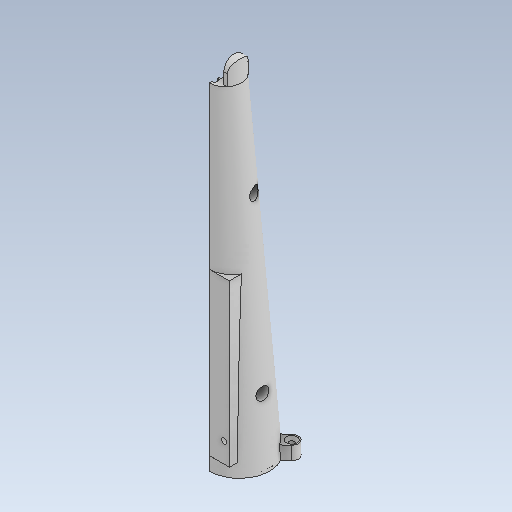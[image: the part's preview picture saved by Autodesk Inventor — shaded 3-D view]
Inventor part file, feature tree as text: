
AUTODESK INVENTOR PART (.ipt)
format: ipt  version: 2021 (Build 250183000, 183)  size: 1,118,208 bytes
history: native  units: mm
features: sketch x40, extrude x38, plane x17, fillet x9, hole x3, thread x3, loft x2, revolve x2, other x1
ambient origin geometry x8: Origin, YZ Plane, XZ Plane, XY Plane, X Axis, Y Axis, Z Axis, Center Point
bodies: Body1 (feature_tree)
feature tree (115):
  other  "Sólido1"
  plane  "Plano de trabajo1"
  plane  "Plano de trabajo2"
  plane  "Plano de trabajo4"
  plane  "Plano de trabajo5"
  plane  "Plano de trabajo6"
  sketch  "Boceto1"  dims[d1=250.0mm d2=0.0mm d3=-80.0mm d4=-110.0mm]
  sketch  "Boceto2"  dims[d5=-140.0mm d7=-0.0mm d8=2.0mm]
  sketch  "Boceto3"  dims[d9=140.0mm d10=250.0mm]
  sketch  "Boceto4"  dims[d11=24.0mm d22=0.0mm d23=90.0deg d24=0.0mm d25=90.0deg]
  sketch  "Boceto6"  dims[d44=45.0mm d49=29.11157mm]
  sketch  "Boceto7"  dims[d50=29.11157mm d53=29.11157mm]
  loft  "Solevación1"
  fillet  "Empalme2"  [1 undecoded]
  extrude  "Extrusión1"  TaperAngle=0.0deg  [1 undecoded]
  fillet  "Empalme5"  Radius=2.0mm
  plane  "Plano de trabajo7"
  extrude  "Extrusión2"  Depth=250.0mm
  plane  "Plano de trabajo8"
  plane  "Plano de trabajo9"
  loft  "Solevación9"
  plane  "Plano de trabajo10"
  extrude  "Extrusión3"  Depth=29.11157mm
  plane  "Plano de trabajo11"
  revolve  "Revolución1"  [1 undecoded]
  revolve  "Revolución2"  [1 undecoded]
  extrude  "Extrusión4"  Depth=32.5mm
  plane  "Plano de trabajo12"
  extrude  "Extrusión5"  Depth=44.747934mm
  plane  "Plano de trabajo13"
  plane  "Plano de trabajo14"
  extrude  "Extrusión6"  Depth=42.747934mm
  extrude  "Extrusión7"  Depth=42.747934mm
  extrude  "Extrusión8"  Depth=13.0mm
  extrude  "Extrusión11"  Depth=6.5mm
  extrude  "Extrusión9"  Depth=7.75mm
  extrude  "Extrusión10"  Depth=16.0mm
  extrude  "Extrusión12"  Depth=12.0mm
  sketch  "Boceto30"  dims[d160=-19.75mm d161=0.0mm]
  extrude  "Extrusión13"  Depth=7.75mm
  extrude  "Extrusión14"  Depth=6.5mm
  extrude  "Extrusión15"  TaperAngle=0.0deg  [1 undecoded]
  hole  "Agujero1"  [1 undecoded]
  thread  "Rosca1"  [1 undecoded]
  extrude  "Extrusión16"  Depth=2.0mm
  plane  "Plano de trabajo16"
  extrude  "Extrusión17"  TaperAngle=0.0deg  [1 undecoded]
  extrude  "Extrusión18"  TaperAngle=0.0deg  [1 undecoded]
  plane  "Plano de trabajo17"
  sketch  "Boceto46"  dims[d185=2.0mm d187=1.0mm]
  hole  "Agujero2"  [1 undecoded]
  hole  "Agujero3"  [1 undecoded]
  plane  "Plano de trabajo19"
  sketch  "Boceto50"  dims[d193=0.25mm d194=90.0deg]
  extrude  "Extrusión22"  Depth=12.0mm
  extrude  "Extrusión23"  [1 undecoded]
  extrude  "Extrusión24"  Depth=0.75mm
  plane  "Plano de trabajo20"
  extrude  "Extrusión25"  Depth=1.0mm
  fillet  "Empalme6"  Radius=11.0mm
  fillet  "Empalme7"  Radius=17.453293mm
  sketch  "Boceto49"  dims[d191=2.0mm d192=0.25mm]
  extrude  "Extrusión29"  Depth=0.75mm
  extrude  "Extrusión30"  Depth=0.25mm
  sketch  "Boceto44"  dims[d181=0.75mm d182=0.25mm]
  sketch  "Boceto47"  dims[d189=3.0mm d190=2.0mm]
  extrude  "Extrusión26"  Depth=0.25mm
  extrude  "Extrusión27"  Depth=2.0mm
  extrude  "Extrusión28"  Depth=2.0mm
  sketch  "Boceto45"  dims[d183=1.0mm d184=0.25mm]
  extrude  "Extrusión31"  Depth=2.0mm
  extrude  "Extrusión32"  TaperAngle=90.0deg  [1 undecoded]
  extrude  "Extrusión33"  [1 undecoded]
  extrude  "Extrusión34"  Depth=20.0mm
  extrude  "Extrusión35"  Depth=2.0mm
  thread  "Rosca2"  [1 undecoded]
  thread  "Rosca3"  [1 undecoded]
  fillet  "Empalme8"  [1 undecoded]
  fillet  "Empalme9"  Radius=0.5mm
  fillet  "Empalme10"  Radius=0.25mm
  fillet  "Empalme11"  [1 undecoded]
  extrude  "Extrusión36"  Depth=1.8mm TaperAngle=0.0deg
  extrude  "Extrusión37"  Depth=1.8mm TaperAngle=0.0deg
  fillet  "Empalme12"  Radius=2.0mm
  sketch  "Boceto54"  dims[d201=9.0mm d202=9.0mm d203=2.0mm d204=201.65mm d205=0.0mm d206=0.5mm d207=0.25mm d208=-7.5mm]
  extrude  "Agujero_tornillo_caja"  Depth=1.8mm
  extrude  "Extrusión40"  Depth=6.5mm
  extrude  "Test_section"  Depth=1.8mm
  extrude  "Extrusión41"  Depth=1.8mm
  sketch  "Boceto55"  dims[d209=100.0mm d210=0.0mm d211=35.0mm d212=0.0mm d213=210.0mm d214=0.0mm d215=2.0mm d216=1.059493mm d217=6.5mm d218=1.059493mm d219=5.0mm d220=2.0mm d221=0.0mm d222=2.0mm d223=6.5mm d224=1.059493mm d225=5.0mm d226=4.85mm d227=2.0mm d228=0.0mm d229=6.0mm d230=10.0mm d231=3.0mm d232=11.0mm d233=10.5mm d235=30.0deg d236=4.75mm d237=0.0mm d238=-17.0mm d239=100.0mm d240=0.0mm d241=6.5mm d242=1.65mm d243=3.3mm d244=15.6mm d245=2.0mm d247=16.0mm d248=2.0mm d249=0.0mm d250=4.5mm d251=0.75mm d252=2.5mm d253=1.0mm d254=11.0mm d255=17.453293mm d256=2.939597mm d257=0.75mm d258=0.75mm d259=0.25mm d260=1.0mm d261=0.25mm d262=2.0mm d263=1.0mm d264=3.0mm d265=2.0mm d266=2.0mm d267=0.25mm d268=0.25mm d269=40.0mm d270=1.0mm d271=1.0mm d272=7.75mm d273=0.5mm d274=8.5mm d275=90.0deg d276=0.0mm d277=17.75mm d280=22.5mm d281=2.0mm d282=0.0mm d283=0.0mm d292=2.0mm d293=0.0mm d296=3.5mm d297=0.0mm d299=4.0mm d300=3.708mm d301=3.023mm d302=2.0mm d303=14.3117mm d304=16.0mm d305=0.0mm d306=16.0mm d307=0.0mm d314=6.0mm d315=19.2mm d316=6.0mm d317=19.2mm d318=13.0mm d320=6.0mm d321=19.2mm d322=13.0mm d323=6.0mm d324=19.2mm d325=13.0mm d326=7.0mm d332=10.0mm d333=0.0mm d335=-41.6mm d336=4.0mm d337=1.0mm d338=9.0mm d339=4.0mm d340=1.0mm d341=9.0mm d342=4.0mm d343=5.2mm d344=6.0mm d345=0.0mm d346=15.0mm d347=5.0mm d349=5.0mm d351=0.0mm d352=45.0mm d354=10.0mm d355=10.0mm d356=0.0mm d357=15.0mm d358=0.0mm d359=2.0mm d363=50.4125mm d376=14.059493mm d377=2.0mm d378=0.0mm d379=2.0mm d380=11.25mm d381=90.0mm d382=290.0mm d383=14.059493mm d384=100.825mm d390=30.940507mm d391=2.0mm d392=100.825mm d393=14.790546mm d394=2.0mm d395=3.0mm d396=6.0mm d397=4.0mm d398=4.0mm d399=4.0mm d400=8.128453mm d401=12.0mm d402=4.45mm d403=2.5mm d404=1.65mm d405=1.65mm d406=1.0mm d407=2.0mm d408=2.0mm d409=0.0mm d411=50.4125mm d412=6.0mm d418=13.059493mm d419=6.5mm d420=6.5mm d421=50.4125mm d422=126.03125mm d423=0.0mm d424=15.0mm d425=5.0mm d426=5.0mm d427=0.0mm d428=45.0mm d429=10.0mm d430=2.0mm d431=4.0mm d432=6.0mm d433=8.0mm d434=2.0mm d435=90.0deg d436=20.0mm d437=0.0mm d438=4.0mm d439=6.0mm d440=8.0mm d441=2.0mm d442=90.0deg d443=20.0mm d444=0.0mm d446=10.0mm d447=3.0mm d448=11.0mm d450=9.2mm d451=9.2mm d452=90.0mm d453=750.0mm d454=22.5mm d455=43.0mm d456=44.0mm d457=14.059493mm d458=11.25mm d461=22.5mm d462=43.0mm d463=7.059493mm d464=3.0mm d465=6.0mm d466=3.0mm d467=6.0mm d468=45.0mm d469=130.0mm d470=17.04mm d471=30.0mm d472=15.0mm d473=0.0mm d474=1.5mm d475=2.0mm d476=1.5mm d477=2.0mm d478=120.0mm d479=0.0mm d480=120.0mm d481=0.0mm d482=116.0mm d483=0.0mm d484=69.0mm d485=0.0mm d486=-1.5mm d487=65.395511mm d488=2.6mm d489=60.0deg d490=45.0deg d491=15.0mm d492=1.6mm d493=0.0mm d494=180.0mm d495=0.0mm d496=180.0mm d497=0.0mm d498=2.0mm d499=0.0mm d500=4.1mm d501=4.4mm d502=10.0mm d503=0.0mm d504=7.0mm d505=0.0mm d506=7.0mm d507=0.0mm d508=4.4mm d509=4.4mm d510=4.4mm d511=7.0mm d512=0.0mm d513=25.497mm d514=0.0mm d515=0.0mm d516=0.0mm d517=4.0mm d518=4.0mm d519=2.0mm d520=0.0mm d521=2.0mm d522=0.0mm d523=2.0mm d524=0.0mm d525=1.0mm d526=0.8mm d527=1.0mm d528=0.8mm d533=3.0mm d534=1.5mm d537=1.0mm d538=6.5mm d539=3.0mm d540=1.5mm d541=0.0mm d542=0.0mm d543=2.0mm d544=0.0mm d545=2.5mm d546=135.0mm d547=4.0mm d548=130.0mm d549=0.0mm d550=0.0mm d551=25.0mm d552=11.0mm d553=4.0mm d554=6.0mm d555=12.0mm d556=0.0mm d557=10.0mm d558=0.0mm d559=1.2mm d560=1.8mm d561=0.0mm]
  sketch  "Boceto9"  dims[d59=29.11157mm d61=29.11157mm]
  sketch  "Boceto10"  dims[d65=22.5mm d66=32.5mm]
  sketch  "Boceto15"  dims[d67=22.5mm d90=44.747934mm]
  sketch  "Boceto16"  dims[d91=42.747934mm d93=42.747934mm]
  sketch  "Boceto17"  dims[d96=0.0mm d97=90.0deg d98=0.0mm d99=90.0deg d100=0.0mm d101=90.0deg d102=0.0mm d103=90.0deg d112=42.747934mm]
  sketch  "Boceto18"  dims[d115=5.0mm d120=13.0mm]
  sketch  "Boceto19"  dims[d121=6.5mm d124=7.75mm]
  sketch  "Boceto20"  dims[d125=7.75mm d126=7.75mm]
  sketch  "Boceto21"  dims[d127=7.75mm d130=16.0mm]
  sketch  "Boceto22"  dims[d131=0.0mm d132=12.0mm]
  sketch  "Boceto24"  dims[d133=12.0mm d134=7.75mm]
  sketch  "Boceto25"  dims[d135=6.5mm d136=7.75mm]
  sketch  "Boceto26"  dims[d137=15.0mm d138=0.0mm]
  sketch  "Boceto27"  dims[d146=-8.5mm d147=30.0mm d148=2.0mm]
  sketch  "Boceto28"  dims[d149=25.12mm d150=2.0mm]
  sketch  "Boceto29"  dims[d151=10.357mm d156=0.0mm d157=90.0deg d158=0.0mm d159=90.0deg]
  sketch  "Boceto31"  dims[d163=0.0mm d164=2.0mm]
  sketch  "Boceto36"  dims[d165=15.0mm d166=4.0mm]
  sketch  "Boceto37"  dims[d167=30.0mm d168=12.0mm]
  sketch  "Boceto38"  dims[d169=0.0mm d170=-7.25mm]
  sketch  "Boceto39"  dims[d171=4.5mm d172=0.75mm]
  sketch  "Boceto40"  dims[d173=2.5mm d174=1.0mm d176=11.0mm d177=17.453293mm]
  sketch  "Boceto41"  dims[d179=2.939597mm d180=0.75mm]
  sketch  "Boceto51"  dims[d196=4.381635mm d197=0.0mm d198=-48.35mm]
  sketch  "Boceto53"  dims[d199=12.0mm d200=20.0mm]
note: 18 required parameter values undecoded (feature->parameter linkage not recoverable at this tier; creation-order binding heuristic only, values carry confidence <= 0.55)